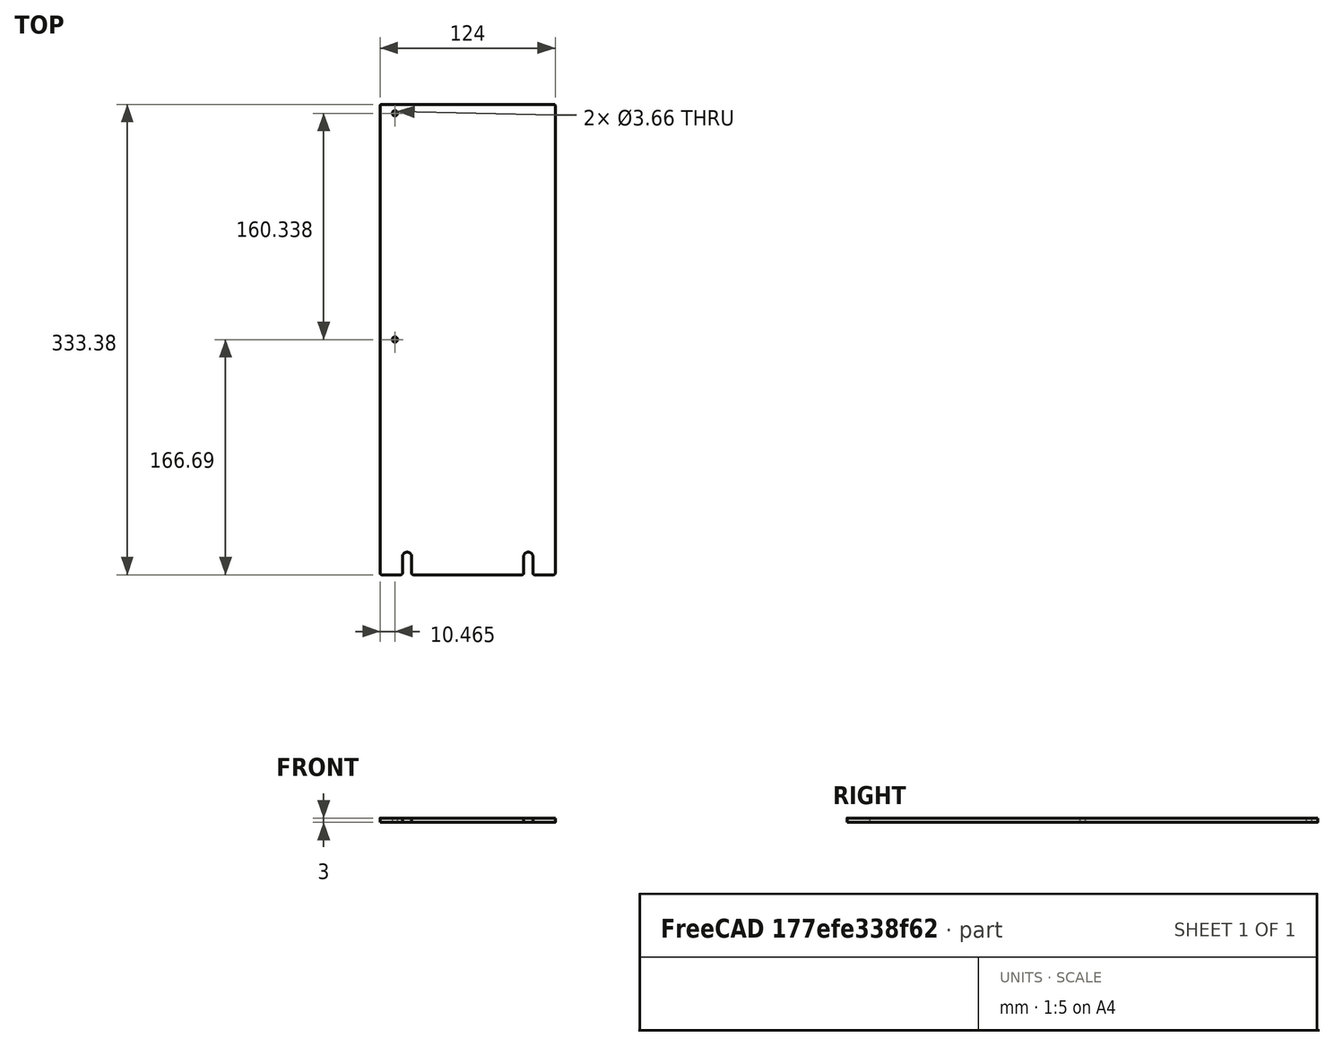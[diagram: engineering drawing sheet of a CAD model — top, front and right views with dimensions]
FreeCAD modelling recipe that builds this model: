
FCSTD DOCUMENT  (FreeCAD 0.21R33675 (Git))
Label: sleep_box_front_back
License: All rights reserved
LicenseURL: http://en.wikipedia.org/wiki/All_rights_reserved
objects: Sketcher::SketchObject×1, Spreadsheet::Sheet×1, PartDesign::Pad×1, PartDesign::Body×1
note: 4 computed .brp shape members not serialized (recipe doc carries the construction recipe); baked Part::Feature solids carry a one-line shape summary decoded from their .brp

FEATURE [Sketcher::SketchObject] Sketch
  FullyConstrained = true
  MapMode = 5
  Support = -> [XY_Plane]
  expr: Constraints[19] = Spreadsheet.FilletRadius
  expr: Constraints[21] = Spreadsheet.Height
  expr: Constraints[22] = Spreadsheet.Length
  expr: Constraints[29] = Spreadsheet.MountHoleSideMargin
  expr: Constraints[35] = Spreadsheet.MountHoleDistanceFromBottom
  expr: Constraints[38] = Spreadsheet.MountHoleDiameter
  expr: Constraints[42] = Spreadsheet.MountHoleSideMargin
  expr: Constraints[50] = Spreadsheet.BracketHoleFromSide
  expr: Constraints[51] = Spreadsheet.UpperBracketHoleFromTop
  expr: Constraints[55] = Spreadsheet.BracketHoleDiameter
  sketch-geometry (35):
    g0: ArcOfCircle CenterX=-61 CenterY=165.687 CenterZ=0 NormalX=0 NormalY=0 NormalZ=1 AngleXU=0 Radius=1 StartAngle=1.5708 EndAngle=3.14159
    g1: LineSegment StartX=-61 StartY=166.687 StartZ=0 EndX=61 EndY=166.687 EndZ=0
    g2: ArcOfCircle CenterX=61 CenterY=165.687 CenterZ=0 NormalX=0 NormalY=0 NormalZ=1 AngleXU=0 Radius=1 StartAngle=-1.15e-14 EndAngle=1.5708
    g3: LineSegment StartX=62 StartY=165.687 StartZ=0 EndX=62 EndY=-165.688 EndZ=0
    g4: ArcOfCircle CenterX=61 CenterY=-165.688 CenterZ=0 NormalX=0 NormalY=0 NormalZ=1 AngleXU=0 Radius=1 StartAngle=4.71239 EndAngle=6.28319
    g5: LineSegment StartX=61 StartY=-166.688 StartZ=0 EndX=-61 EndY=-166.688 EndZ=0
    g6: ArcOfCircle CenterX=-61 CenterY=-165.688 CenterZ=0 NormalX=0 NormalY=0 NormalZ=1 AngleXU=0 Radius=1 StartAngle=3.14159 EndAngle=4.71239
    g7: LineSegment StartX=-62 StartY=-165.688 StartZ=0 EndX=-62 EndY=165.688 EndZ=0
    g8: GeomPoint X=-62 Y=166.687 Z=0
    g9: GeomPoint X=62 Y=-166.688 Z=0
    g10: LineSegment StartX=-42.95 StartY=-153.987 StartZ=0 EndX=-62 EndY=-153.987 EndZ=0
    g11: LineSegment StartX=42.95 StartY=-153.987 StartZ=0 EndX=62 EndY=-153.987 EndZ=0
    g12: Circle CenterX=-42.95 CenterY=-153.987 CenterZ=0 NormalX=0 NormalY=0 NormalZ=1 AngleXU=0 Radius=3.302
    g13: Circle CenterX=42.95 CenterY=-153.987 CenterZ=0 NormalX=0 NormalY=0 NormalZ=1 AngleXU=0 Radius=3.302
    g14: LineSegment StartX=0 StartY=-153.987 StartZ=0 EndX=0 EndY=-166.688 EndZ=0
    g15: LineSegment StartX=-42.95 StartY=-153.987 StartZ=0 EndX=0 EndY=-153.987 EndZ=0
    g16: LineSegment StartX=0 StartY=-153.987 StartZ=0 EndX=42.95 EndY=-153.987 EndZ=0
    g17: LineSegment StartX=-51.5352 StartY=166.687 StartZ=0 EndX=-51.5352 EndY=160.337 EndZ=0
    g18: LineSegment StartX=-51.5352 StartY=160.337 StartZ=0 EndX=-51.5352 EndY=0 EndZ=0
    g19: LineSegment StartX=-51.5352 StartY=5.7e-15 StartZ=0 EndX=-62 EndY=5.7e-15 EndZ=0
    g20: Circle CenterX=-51.5352 CenterY=160.337 CenterZ=0 NormalX=0 NormalY=0 NormalZ=1 AngleXU=0 Radius=1.8288
    g21: Circle CenterX=-51.5352 CenterY=5.7e-15 CenterZ=0 NormalX=0 NormalY=0 NormalZ=1 AngleXU=0 Radius=1.8288
    g22: ArcOfCircle CenterX=-42.95 CenterY=-153.987 CenterZ=0 NormalX=0 NormalY=0 NormalZ=1 AngleXU=0 Radius=3.302 StartAngle=0 EndAngle=3.14159
    g23: LineSegment StartX=-46.252 StartY=-153.987 StartZ=0 EndX=-46.252 EndY=-165.688 EndZ=0
    g24: LineSegment StartX=-39.648 StartY=-153.987 StartZ=0 EndX=-39.648 EndY=-165.688 EndZ=0
    g25: ArcOfCircle CenterX=-47.252 CenterY=-165.688 CenterZ=0 NormalX=0 NormalY=0 NormalZ=1 AngleXU=0 Radius=1 StartAngle=4.71239 EndAngle=6.28319
    g26: ArcOfCircle CenterX=-38.648 CenterY=-165.688 CenterZ=0 NormalX=0 NormalY=0 NormalZ=1 AngleXU=0 Radius=1 StartAngle=3.14159 EndAngle=4.71239
    g27: ArcOfCircle CenterX=42.95 CenterY=-153.987 CenterZ=0 NormalX=0 NormalY=0 NormalZ=1 AngleXU=0 Radius=3.302 StartAngle=7.9e-15 EndAngle=3.14159
    g28: LineSegment StartX=39.648 StartY=-153.988 StartZ=0 EndX=39.648 EndY=-165.688 EndZ=0
    g29: LineSegment StartX=46.252 StartY=-153.987 StartZ=0 EndX=46.252 EndY=-165.688 EndZ=0
    g30: ArcOfCircle CenterX=38.648 CenterY=-165.688 CenterZ=0 NormalX=0 NormalY=0 NormalZ=1 AngleXU=0 Radius=1 StartAngle=4.71239 EndAngle=6.28319
    g31: ArcOfCircle CenterX=47.252 CenterY=-165.688 CenterZ=0 NormalX=0 NormalY=0 NormalZ=1 AngleXU=0 Radius=1 StartAngle=3.14159 EndAngle=4.71239
    g32: LineSegment StartX=-61 StartY=-166.688 StartZ=0 EndX=-47.252 EndY=-166.688 EndZ=0
    g33: LineSegment StartX=-38.648 StartY=-166.687 StartZ=0 EndX=38.648 EndY=-166.688 EndZ=0
    g34: LineSegment StartX=47.252 StartY=-166.688 StartZ=0 EndX=61 EndY=-166.688 EndZ=0
  constraints (90):
    c: Tangent(g0,g1) = 1.5708
    c: Tangent(g1,g2) = 1.5708
    c: Tangent(g2,g3) = 1.5708
    c: Tangent(g3,g4) = 1.5708
    c: Tangent(g4,g5) = 1.5708
    c: Tangent(g5,g6) = 1.5708
    c: Tangent(g6,g7) = 1.5708
    c: Tangent(g7,g0) = 1.5708
    c: Horizontal(g1)
    c: Horizontal(g5)
    c: Vertical(g3)
    c: Vertical(g7)
    c: Equal(g0,g2)
    c: Equal(g2,g4)
    c: Equal(g4,g6)
    c: PointOnObject(g8,g1)
    c: PointOnObject(g8,g7)
    c: PointOnObject(g9,g3)
    c: PointOnObject(g9,g5)
    c: Radius(g2) = 1
    c: Symmetric(g8,g9,g-1)
    c: DistanceY(g4,g1) = 333.375
    c: DistanceX(g0,g2) = 124
    c: PointOnObject(g14,g5)
    c: PointOnObject(g14,g-2)
    c: PointOnObject(g10,g7)
    c: Horizontal(g10)
    c: PointOnObject(g11,g3)
    c: Horizontal(g11)
    c: DistanceX(g10,g10) = 19.05
    c: Vertical(g14)
    c: Coincident(g15,g12)
    c: Horizontal(g15)
    c: Coincident(g16,g13)
    c: Horizontal(g16)
    c: DistanceY(g14,g14) = 12.7
    c: Coincident(g10,g12)
    c: Coincident(g13,g11)
    c: Diameter(g13) = 6.604
    c: Coincident(g16,g14)
    c: Coincident(g15,g14)
    c: Equal(g12,g13)
    c: DistanceX(g11,g11) = 19.05
    c: PointOnObject(g17,g1)
    c: Vertical(g17)
    c: Coincident(g18,g17)
    c: Vertical(g18)
    c: Coincident(g19,g18)
    c: Horizontal(g19)
    c: Symmetric(g0,g6,g19)
    c: DistanceX(g8,g17) = 10.4648
    c: DistanceY(g17,g17) = 6.35
    c: Coincident(g20,g17)
    c: Coincident(g21,g18)
    c: Equal(g21,g20)
    c: Diameter(g20) = 3.6576
    c: Coincident(g22,g10)
    c: PointOnObject(g22,g10)
    c: PointOnObject(g22,g15)
    c: PointOnObject(g22,g12)
    c: Coincident(g23,g22)
    c: Vertical(g23)
    c: Coincident(g24,g22)
    c: Vertical(g24)
    c: Equal(g23,g24)
    c: Tangent(g25,g23) = 1.5708
    c: Tangent(g25,g5) = 1.5708
    c: Tangent(g26,g24) = -1.5708
    c: Tangent(g26,g5) = 1.5708
    c: Equal(g25,g6)
    c: Coincident(g27,g11)
    c: PointOnObject(g27,g16)
    c: PointOnObject(g27,g11)
    c: PointOnObject(g27,g13)
    c: Coincident(g28,g27)
    c: Vertical(g28)
    c: Coincident(g29,g27)
    c: Vertical(g29)
    c: Equal(g28,g29)
    c: Tangent(g30,g28) = 1.5708
    c: Tangent(g30,g5) = 1.5708
    c: Tangent(g31,g29) = -1.5708
    c: Tangent(g31,g5) = 1.5708
    c: Equal(g31,g4)
    c: Coincident(g32,g6)
    c: Coincident(g32,g25)
    c: Coincident(g33,g26)
    c: Coincident(g33,g30)
    c: Coincident(g34,g31)
    c: Coincident(g34,g4)
FEATURE [Spreadsheet::Sheet] Spreadsheet
  cells = A2='Parameters; A3='BeamHeight; B3(BeamHeight)==1 in; A4='FloorHeight; B4(FloorHeight)==BeamHeight + 0.125 in; A5='HeightAboveFloor; B5(HeightAboveFloor)==12 in; A6='Height; B6(Height)==HeightAboveFloor + FloorHeight; A7='Length; B7(Length)==124 mm; A8='Thickness; B8(Thickness)==3 mm; A9='FilletRadius; B9(FilletRadius)==1 mm; A10='MountHoleDiameter; B10(MountHoleDiameter)==0.26 in; A11='MountHoleDistanceFromBottom; B11(MountHoleDistanceFromBottom)==0.5 in; A12='MountHoleSideMargin; B12(MountHoleSideMargin)==0.75 in; A14='BracketWidth; B14(BracketWidth)==0.5 in; A15='BracketHoleDiameter; B15(BracketHoleDiameter)==0.144 in; A16='BracketHoleOffset; B16(BracketHoleOffset)==0.412 in; A17='UpperBracketHoleFromTop; B17(UpperBracketHoleFromTop)==0.5 * BracketWidth; A18='BracketHoleFromSide; B18(BracketHoleFromSide)==BracketHoleOffset
FEATURE [PartDesign::Pad] Pad
  Direction = (0,0,1)
  Length = 3
  Length2 = 10
  Profile = -> Sketch
  ReferenceAxis = -> Sketch [N_Axis]
  Type = 0
  expr: Length = Spreadsheet.Thickness
FEATURE [PartDesign::Body] Body
  Group = -> [Sketch,Pad]
  Origin = -> Origin
  Tip = -> Pad
